# Revit family: C24
name_source: partatom
category: Lighting Fixtures
revit_build: Autodesk Revit 2014 (Build: 20130308_1515(x64)
units: mm (PartAtom-declared; Revit-internal decimal feet)

## types (1)
- C24
    Apparent Load = 11 VA
    Body = Hubbell-Metal_Copper
    Color Filter = 16777215
    Default Elevation = 48 "
    Description = the Spun Copper Bullet has a unique swivel mount that provides superior aiming without loosening over time
    Dimming Lamp Color Temperature Shift = <None>
    Emit Shape Visible in Rendering = No
    Emit from Circle Diameter = 3 "
    LED = Glass - Hubbell - White
    Lamp = LED
    Led Surface = Paint - Hubbell - Matte White
    Manufacturer = Kim Lighting A unit of Hubbell Lighting
    Model = C24
    Mounting = Metal-Hubbell-Brass
    Photometric Web File = c24f3-9l3k.ies
    Product Documentation Link = https://hubbellcdn.com
    Product page Link = https://www.hubbell.com
    Tilt Angle = -180.00°
    Type Comments = Spun Copper Bullet
    URL = https://www.hubbell.com
    Warranty = Limited 5 Years Warranty
    Wattage Comments = 11W

## geometry (parser evidence)
native form markers: Sweep x1
no freeform markers — native parametric forms only
